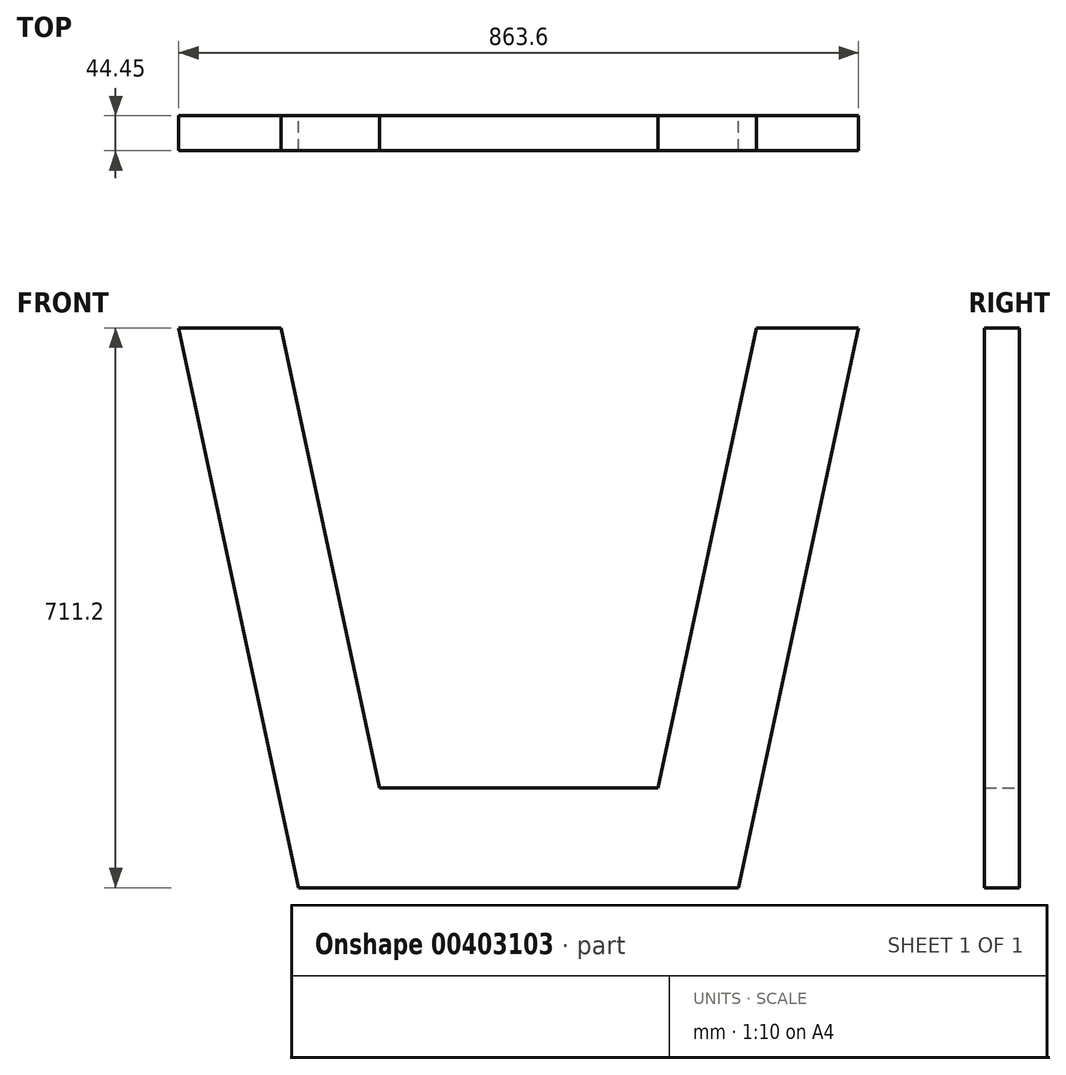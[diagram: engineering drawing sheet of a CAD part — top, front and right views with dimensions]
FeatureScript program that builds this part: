
annotation { "Feature Type Name" : "Feature", "Feature Type Description" : "" }
export const myFeature = defineFeature(function(context is Context, id is Id, definition is map)
    precondition{}
    {
        {
            var Q0;
            Q0=qCreatedBy(makeId("Front.planeOp"),FACE);
            var sketch = newSketch(context, id + "F0", { "sketchPlane" : qUnion([Q0])});
            skLineSegment(sketch, "E0", {"start": v(-431.8, 0) * mm, "end": v(-301.92, 0) * mm});
            skLineSegment(sketch, "E1", {"start": v(-301.92, 0) * mm, "end": v(-176.73, -584.2) * mm});
            skLineSegment(sketch, "E2", {"start": v(-176.73, -584.2) * mm, "end": v(176.73, -584.2) * mm});
            skLineSegment(sketch, "E3", {"start": v(176.73, -584.2) * mm, "end": v(301.92, 0) * mm});
            skLineSegment(sketch, "E4", {"start": v(301.92, 0) * mm, "end": v(431.8, 0) * mm});
            skLineSegment(sketch, "E5", {"start": v(431.8, 0) * mm, "end": v(279.4, -711.2) * mm});
            skLineSegment(sketch, "E6", {"start": v(279.4, -711.2) * mm, "end": v(-279.4, -711.2) * mm});
            skLineSegment(sketch, "E7", {"start": v(-279.4, -711.2) * mm, "end": v(-431.8, 0) * mm});
            skLineSegment(sketch, "E8", {"start": v(0, 0) * mm, "end": v(0, -584.2) * mm, "construction": true});
            skLineSegment(sketch, "E9", {"start": v(0, -584.2) * mm, "end": v(0, -711.2) * mm, "construction": true});
            skSolve(sketch);
        }
        {
            var Q0;
            Q0 = qSketchRegion(id + "F0", true);
            extrude(context, id + "F1", {"entities" : qUnion([Q0]), "depth" : 44.45 * mm});
        }
    });
